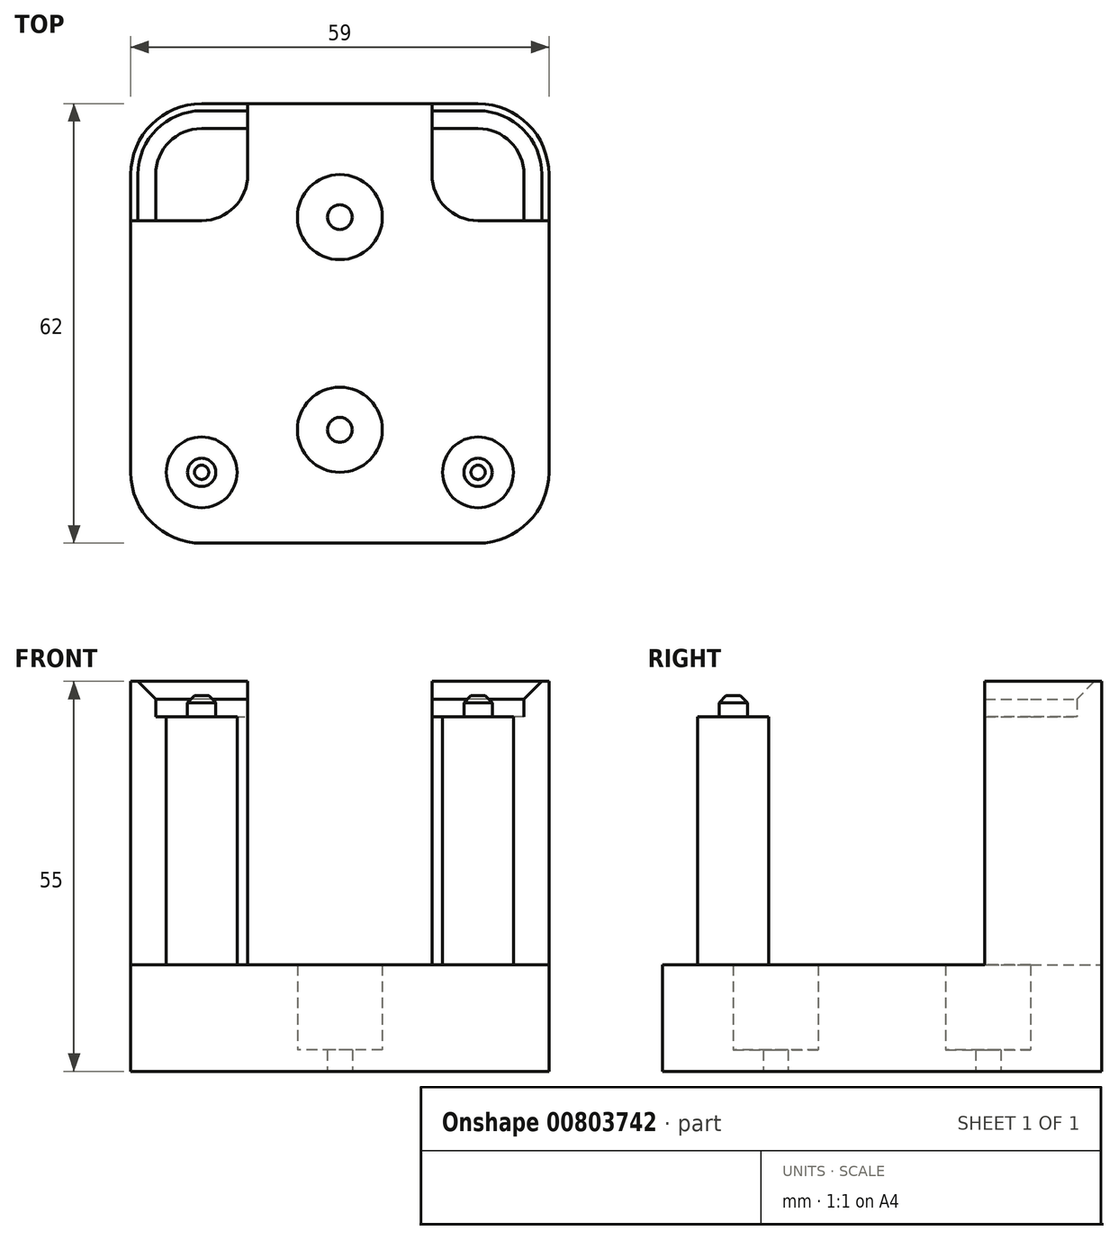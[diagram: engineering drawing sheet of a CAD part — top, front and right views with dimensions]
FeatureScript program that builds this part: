
annotation { "Feature Type Name" : "Feature", "Feature Type Description" : "" }
export const myFeature = defineFeature(function(context is Context, id is Id, definition is map)
    precondition{}
    {
        {
            var Q0;
            Q0=qCreatedBy(makeId("Top.planeOp"),FACE);
            var sketch = newSketch(context, id + "F0", { "sketchPlane" : qUnion([Q0])});
            skLineSegment(sketch, "E0.bottom", {"start": v(19.5, 31) * mm, "end": v(-19.5, 31) * mm});
            skLineSegment(sketch, "E0.top", {"start": v(19.5, -31) * mm, "end": v(-19.5, -31) * mm});
            skLineSegment(sketch, "E0.left", {"start": v(29.5, 21) * mm, "end": v(29.5, -21) * mm});
            skLineSegment(sketch, "E0.right", {"start": v(-29.5, 21) * mm, "end": v(-29.5, -21) * mm});
            skPoint(sketch, "E0.middle", {"position": v(0, 0) * mm});
            skCircle(sketch, "E1", {"center": v(19.5, -21) * mm, "radius": 2 * mm});
            skCircle(sketch, "E2", {"center": v(-19.5, 21) * mm, "radius": 6.5 * mm});
            skCircle(sketch, "E3", {"center": v(19.5, -21) * mm, "radius": 5 * mm});
            skLineSegment(sketch, "E4", {"start": v(0, 0) * mm, "end": v(0, 15) * mm});
            skCircle(sketch, "E5", {"center": v(0, 15) * mm, "radius": 6 * mm});
            skCircle(sketch, "E6", {"center": v(0, 15) * mm, "radius": 1.75 * mm});
            skLineSegment(sketch, "E7", {"start": v(0, 0) * mm, "end": v(0, -15) * mm});
            skCircle(sketch, "E8", {"center": v(0, -15) * mm, "radius": 6 * mm});
            skCircle(sketch, "E9", {"center": v(0, -15) * mm, "radius": 1.75 * mm});
            skLineSegment(sketch, "E10.bottom", {"start": v(-19.5, 21) * mm, "end": v(19.5, 21) * mm});
            skLineSegment(sketch, "E10.top", {"start": v(-19.5, -21) * mm, "end": v(19.5, -21) * mm});
            skLineSegment(sketch, "E10.left", {"start": v(-19.5, 21) * mm, "end": v(-19.5, -21) * mm});
            skLineSegment(sketch, "E10.right", {"start": v(19.5, 21) * mm, "end": v(19.5, -21) * mm});
            skLineSegment(sketch, "E11", {"start": v(0, 0) * mm, "end": v(19.5, 0) * mm});
            skPoint(sketch, "E12.visualSharp", {"position": v(-29.5, 31) * mm});
            skArc(sketch, "E12.filletArc", {"start": v(-19.5, 31) * mm, "mid": v(-26.57, 28.07) * mm, "end": v(-29.5, 21) * mm});
            skPoint(sketch, "E13.visualSharp", {"position": v(29.5, 31) * mm});
            skArc(sketch, "E13.filletArc", {"start": v(29.5, 21) * mm, "mid": v(26.57, 28.07) * mm, "end": v(19.5, 31) * mm});
            skPoint(sketch, "E14.visualSharp", {"position": v(-29.5, -31) * mm});
            skArc(sketch, "E14.filletArc", {"start": v(-29.5, -21) * mm, "mid": v(-26.57, -28.07) * mm, "end": v(-19.5, -31) * mm});
            skPoint(sketch, "E15.visualSharp", {"position": v(29.5, -31) * mm});
            skArc(sketch, "E15.filletArc", {"start": v(19.5, -31) * mm, "mid": v(26.57, -28.07) * mm, "end": v(29.5, -21) * mm});
            skLineSegment(sketch, "E16", {"start": v(-19.5, 27.5) * mm, "end": v(19.5, 27.5) * mm});
            skLineSegment(sketch, "E17", {"start": v(-19.5, 14.5) * mm, "end": v(19.5, 14.5) * mm});
            skLineSegment(sketch, "E18", {"start": v(-19.5, 14.5) * mm, "end": v(-19.5, 14.5) * mm});
            skCircle(sketch, "E19", {"center": v(-19.5, -21) * mm, "radius": 5 * mm});
            skCircle(sketch, "E20", {"center": v(-19.5, -21) * mm, "radius": 2 * mm});
            skCircle(sketch, "E21", {"center": v(19.5, 21) * mm, "radius": 6.5 * mm});
            skLineSegment(sketch, "E22", {"start": v(-13, 21) * mm, "end": v(-13, 31) * mm});
            skLineSegment(sketch, "E23", {"start": v(13, 21) * mm, "end": v(13, 31) * mm});
            skLineSegment(sketch, "E24", {"start": v(19.5, 14.5) * mm, "end": v(29.5, 14.5) * mm});
            skLineSegment(sketch, "E25", {"start": v(-19.5, 14.5) * mm, "end": v(-29.5, 14.5) * mm});
            skLineSegment(sketch, "E26", {"start": v(26, 21) * mm, "end": v(26, 14.5) * mm});
            skLineSegment(sketch, "E27", {"start": v(-26, 21) * mm, "end": v(-26, 14.5) * mm});
            skPoint(sketch, "E27.endSnap0", {"position": v(-24.5, 14.5) * mm});
            skSolve(sketch);
        }
        {
            var Q0;
            {var subQ0=sQuery(id+"F0.wireOp",EDGE,"E22");var subQ1=sQuery(id+"F0.wireOp",EDGE,"E0.bottom");var subQ2=makeQuery(id+"F0.imprint","INTERSECT",VERTEX,{"derivedFrom":[subQ1,subQ0]});Q0=makeQuery(id+"F0.imprint","IMPRINT",FACE,{"disambiguationData":[TD([[makeQuery(id+"F0.imprint","IMPRINT",EDGE,{"disambiguationData":[TD([[subQ2,1.0]])],"derivedFrom":subQ1}),1.0]])]});}
            var Q1;
            Q1=makeQuery(id+"F0.imprint","IMPRINT",FACE,{"disambiguationData":[TD([[makeQuery(id+"F0.imprint","IMPRINT",EDGE,{"derivedFrom":sQuery(id+"F0.wireOp",EDGE,"E0.top")}),-1.0]])]});
            var Q2;
            {var subQ0=sQuery(id+"F0.wireOp",EDGE,"E11");Q2=makeQuery(id+"F0.imprint","IMPRINT",FACE,{"disambiguationData":[TD([[makeQuery(id+"F0.imprint","IMPRINT",EDGE,{"derivedFrom":subQ0}),1.0]])]});}
            var Q3;
            {var subQ1=sQuery(id+"F0.wireOp",EDGE,"E4");var subQ5=sQuery(id+"F0.wireOp",EDGE,"E5");var subQ6=makeQuery(id+"F0.imprint","INTERSECT",VERTEX,{"derivedFrom":[subQ1,subQ5]});Q3=makeQuery(id+"F0.imprint","IMPRINT",FACE,{"disambiguationData":[TD([[makeQuery(id+"F0.imprint","IMPRINT",EDGE,{"disambiguationData":[TD([[subQ6,1.0]])],"derivedFrom":subQ5}),-1.0]])]});}
            var Q4;
            {var subQ0=sQuery(id+"F0.wireOp",EDGE,"E11");Q4=makeQuery(id+"F0.imprint","IMPRINT",FACE,{"disambiguationData":[TD([[makeQuery(id+"F0.imprint","IMPRINT",EDGE,{"derivedFrom":subQ0}),-1.0]])]});}
            var Q5;
            {var subQ0=sQuery(id+"F0.wireOp",EDGE,"Fgb9CfrY-dhn4-4UBN-2pW2-9sD9XJII3xpJ");Q5=makeQuery(id+"F0.imprint","IMPRINT",FACE,{"disambiguationData":[TD([[makeQuery(id+"F0.imprint","IMPRINT",EDGE,{"derivedFrom":subQ0}),1.0]])]});}
            var Q6;
            {var subQ3=sQuery(id+"F0.wireOp",EDGE,"E19");var subQ5=sQuery(id+"F0.wireOp",EDGE,"bsxKk5JZ-FVBb-cfbX-uEi1-lJpJewRCnain");var subQ6=makeQuery(id+"F0.imprint","INTERSECT",VERTEX,{"derivedFrom":[subQ5,subQ3]});Q6=makeQuery(id+"F0.imprint","IMPRINT",FACE,{"disambiguationData":[TD([[makeQuery(id+"F0.imprint","IMPRINT",EDGE,{"disambiguationData":[TD([[subQ6,1.0]])],"derivedFrom":subQ5}),1.0]])]});}
            var Q7;
            {var subQ0=sQuery(id+"F0.wireOp",EDGE,"E22");var subQ1=sQuery(id+"F0.wireOp",EDGE,"E16");var subQ2=makeQuery(id+"F0.imprint","INTERSECT",VERTEX,{"derivedFrom":[subQ1,subQ0]});Q7=makeQuery(id+"F0.imprint","IMPRINT",FACE,{"disambiguationData":[TD([[makeQuery(id+"F0.imprint","IMPRINT",EDGE,{"disambiguationData":[TD([[subQ2,-1.0]])],"derivedFrom":subQ1}),-1.0]])]});}
            var Q8;
            {var subQ0=sQuery(id+"F0.wireOp",EDGE,"Rvfl0PQZ-DZTq-9wpm-qxsT-ofNjnk88OBcv");var subQ1=sQuery(id+"F0.wireOp",EDGE,"E3");var subQ2=makeQuery(id+"F0.imprint","INTERSECT",VERTEX,{"derivedFrom":[subQ1,subQ0]});Q8=makeQuery(id+"F0.imprint","IMPRINT",FACE,{"disambiguationData":[TD([[makeQuery(id+"F0.imprint","IMPRINT",EDGE,{"disambiguationData":[TD([[subQ2,-1.0]])],"derivedFrom":subQ1}),-1.0]])]});}
            var Q9;
            {var subQ0=sQuery(id+"F0.wireOp",EDGE,"E17");var subQ5=sQuery(id+"F0.wireOp",EDGE,"E5");var subQ6=makeQuery(id+"F0.imprint","INTERSECT",VERTEX,{"disambiguationData":[OD(0.0)],"derivedFrom":[subQ5,subQ0]});Q9=makeQuery(id+"F0.imprint","IMPRINT",FACE,{"disambiguationData":[TD([[makeQuery(id+"F0.imprint","IMPRINT",EDGE,{"disambiguationData":[TD([[subQ6,1.0]])],"derivedFrom":subQ5}),-1.0]])]});}
            var Q10;
            {var subQ0=sQuery(id+"F0.wireOp",EDGE,"E10.bottom");var subQ1=sQuery(id+"F0.wireOp",EDGE,"E5");var subQ2=makeQuery(id+"F0.imprint","INTERSECT",VERTEX,{"derivedFrom":[subQ1,subQ0]});Q10=makeQuery(id+"F0.imprint","IMPRINT",FACE,{"disambiguationData":[TD([[makeQuery(id+"F0.imprint","IMPRINT",EDGE,{"disambiguationData":[TD([[subQ2,1.0]])],"derivedFrom":subQ1}),-1.0]])]});}
            extrude(context, id + "F1", {"entities" : qUnion([Q0, Q1, Q2, Q3, Q4, Q5, Q6, Q7, Q8, Q9, Q10]), "depth" : 15 * mm, "offsetDistance" : 25 * mm});
        }
        {
            var Q0;
            {var subQ0=sQuery(id+"F0.wireOp",EDGE,"E2");var subQ1=makeQuery(id+"F0.imprint","INTERSECT",VERTEX,{"derivedFrom":[subQ0,sQuery(id+"F0.wireOp",EDGE,"E16")]});Q0=makeQuery(id+"F0.imprint","IMPRINT",FACE,{"disambiguationData":[TD([[makeQuery(id+"F0.imprint","IMPRINT",EDGE,{"disambiguationData":[TD([[subQ1,1.0]])],"derivedFrom":subQ0}),1.0]])]});}
            var Q1;
            {var subQ0=sQuery(id+"F0.wireOp",EDGE,"E10.left");var subQ3=sQuery(id+"F0.wireOp",EDGE,"E10.bottom");var subQ5=makeQuery(id+"F0.imprint","INTERSECT",VERTEX,{"derivedFrom":[subQ3,subQ0]});Q1=makeQuery(id+"F0.imprint","IMPRINT",FACE,{"disambiguationData":[TD([[makeQuery(id+"F0.imprint","IMPRINT",EDGE,{"disambiguationData":[TD([[subQ5,-1.0]])],"derivedFrom":subQ3}),-1.0]])]});}
            var Q2;
            {var subQ0=sQuery(id+"F0.wireOp",EDGE,"E16");var subQ1=sQuery(id+"F0.wireOp",EDGE,"E2");var subQ2=makeQuery(id+"F0.imprint","INTERSECT",VERTEX,{"derivedFrom":[subQ1,subQ0]});Q2=makeQuery(id+"F0.imprint","IMPRINT",FACE,{"disambiguationData":[TD([[makeQuery(id+"F0.imprint","IMPRINT",EDGE,{"disambiguationData":[TD([[subQ2,-1.0]])],"derivedFrom":subQ0}),-1.0]])]});}
            var Q3;
            {var subQ0=sQuery(id+"F0.wireOp",EDGE,"E21");var subQ1=makeQuery(id+"F0.imprint","INTERSECT",VERTEX,{"derivedFrom":[sQuery(id+"F0.wireOp",EDGE,"E16"),subQ0]});Q3=makeQuery(id+"F0.imprint","IMPRINT",FACE,{"disambiguationData":[TD([[makeQuery(id+"F0.imprint","IMPRINT",EDGE,{"disambiguationData":[TD([[subQ1,1.0]])],"derivedFrom":subQ0}),1.0]])]});}
            var Q4;
            {var subQ0=sQuery(id+"F0.wireOp",EDGE,"E10.right");var subQ1=sQuery(id+"F0.wireOp",EDGE,"E10.bottom");var subQ2=makeQuery(id+"F0.imprint","INTERSECT",VERTEX,{"derivedFrom":[subQ1,subQ0]});Q4=makeQuery(id+"F0.imprint","IMPRINT",FACE,{"disambiguationData":[TD([[makeQuery(id+"F0.imprint","IMPRINT",EDGE,{"disambiguationData":[TD([[subQ2,1.0]])],"derivedFrom":subQ1}),-1.0]])]});}
            var Q5;
            {var subQ0=sQuery(id+"F0.wireOp",EDGE,"E10.top");var subQ1=sQuery(id+"F0.wireOp",EDGE,"E1");var subQ2=makeQuery(id+"F0.imprint","INTERSECT",VERTEX,{"derivedFrom":[subQ1,subQ0]});Q5=makeQuery(id+"F0.imprint","IMPRINT",FACE,{"disambiguationData":[TD([[makeQuery(id+"F0.imprint","IMPRINT",EDGE,{"disambiguationData":[TD([[subQ2,-1.0]])],"derivedFrom":subQ1}),-1.0]])]});}
            var Q6;
            {var subQ0=sQuery(id+"F0.wireOp",EDGE,"E10.top");var subQ1=sQuery(id+"F0.wireOp",EDGE,"E1");var subQ2=makeQuery(id+"F0.imprint","INTERSECT",VERTEX,{"derivedFrom":[subQ1,subQ0]});Q6=makeQuery(id+"F0.imprint","IMPRINT",FACE,{"disambiguationData":[TD([[makeQuery(id+"F0.imprint","IMPRINT",EDGE,{"disambiguationData":[TD([[subQ2,1.0]])],"derivedFrom":subQ1}),-1.0]])]});}
            var Q7;
            {var subQ0=sQuery(id+"F0.wireOp",EDGE,"E20");var subQ1=sQuery(id+"F0.wireOp",EDGE,"E10.top");var subQ2=makeQuery(id+"F0.imprint","INTERSECT",VERTEX,{"derivedFrom":[subQ1,subQ0]});Q7=makeQuery(id+"F0.imprint","IMPRINT",FACE,{"disambiguationData":[TD([[makeQuery(id+"F0.imprint","IMPRINT",EDGE,{"disambiguationData":[TD([[subQ2,-1.0]])],"derivedFrom":subQ1}),-1.0]])]});}
            var Q8;
            {var subQ0=sQuery(id+"F0.wireOp",EDGE,"E20");var subQ1=sQuery(id+"F0.wireOp",EDGE,"E10.top");var subQ2=makeQuery(id+"F0.imprint","INTERSECT",VERTEX,{"derivedFrom":[subQ1,subQ0]});Q8=makeQuery(id+"F0.imprint","IMPRINT",FACE,{"disambiguationData":[TD([[makeQuery(id+"F0.imprint","IMPRINT",EDGE,{"disambiguationData":[TD([[subQ2,-1.0]])],"derivedFrom":subQ1}),1.0]])]});}
            var Q9;
            {var subQ0=sQuery(id+"F0.wireOp",EDGE,"E21");var subQ1=sQuery(id+"F0.wireOp",EDGE,"E16");var subQ2=makeQuery(id+"F0.imprint","INTERSECT",VERTEX,{"derivedFrom":[subQ1,subQ0]});Q9=makeQuery(id+"F0.imprint","IMPRINT",FACE,{"disambiguationData":[TD([[makeQuery(id+"F0.imprint","IMPRINT",EDGE,{"disambiguationData":[TD([[subQ2,1.0]])],"derivedFrom":subQ1}),-1.0]])]});}
            var Q10;
            {var subQ3=sQuery(id+"F0.wireOp",EDGE,"E26");Q10=makeQuery(id+"F0.imprint","IMPRINT",FACE,{"disambiguationData":[TD([[makeQuery(id+"F0.imprint","IMPRINT",EDGE,{"derivedFrom":subQ3}),-1.0]])]});}
            var Q11;
            {var subQ3=sQuery(id+"F0.wireOp",EDGE,"E27");Q11=makeQuery(id+"F0.imprint","IMPRINT",FACE,{"disambiguationData":[TD([[makeQuery(id+"F0.imprint","IMPRINT",EDGE,{"derivedFrom":subQ3}),1.0]])]});}
            extrude(context, id + "F2", {"entities" : qUnion([Q0, Q1, Q2, Q3, Q4, Q5, Q6, Q7, Q8, Q9, Q10, Q11]), "operationType" : NewBodyOperationType.ADD, "depth" : 50 * mm, "offsetDistance" : 25 * mm});
        }
        {
            var Q0;
            {var subQ0=sQuery(id+"F0.wireOp",EDGE,"E10.left");var subQ1=sQuery(id+"F0.wireOp",EDGE,"E10.top");var subQ2=makeQuery(id+"F0.imprint","INTERSECT",VERTEX,{"derivedFrom":[subQ1,subQ0]});Q0=makeQuery(id+"F0.imprint","IMPRINT",FACE,{"disambiguationData":[TD([[makeQuery(id+"F0.imprint","IMPRINT",EDGE,{"disambiguationData":[TD([[subQ2,-1.0]])],"derivedFrom":subQ1}),-1.0]])]});}
            var Q1;
            {var subQ0=sQuery(id+"F0.wireOp",EDGE,"E10.left");var subQ1=sQuery(id+"F0.wireOp",EDGE,"E10.top");var subQ2=makeQuery(id+"F0.imprint","INTERSECT",VERTEX,{"derivedFrom":[subQ1,subQ0]});Q1=makeQuery(id+"F0.imprint","IMPRINT",FACE,{"disambiguationData":[TD([[makeQuery(id+"F0.imprint","IMPRINT",EDGE,{"disambiguationData":[TD([[subQ2,-1.0]])],"derivedFrom":subQ1}),1.0]])]});}
            var Q2;
            {var subQ0=sQuery(id+"F0.wireOp",EDGE,"E10.top");var subQ1=sQuery(id+"F0.wireOp",EDGE,"E1");var subQ2=makeQuery(id+"F0.imprint","INTERSECT",VERTEX,{"derivedFrom":[subQ1,subQ0]});Q2=makeQuery(id+"F0.imprint","IMPRINT",FACE,{"disambiguationData":[TD([[makeQuery(id+"F0.imprint","IMPRINT",EDGE,{"disambiguationData":[TD([[subQ2,1.0]])],"derivedFrom":subQ1}),1.0]])]});}
            var Q3;
            {var subQ0=sQuery(id+"F0.wireOp",EDGE,"E10.top");var subQ1=sQuery(id+"F0.wireOp",EDGE,"E1");var subQ2=makeQuery(id+"F0.imprint","INTERSECT",VERTEX,{"derivedFrom":[subQ1,subQ0]});Q3=makeQuery(id+"F0.imprint","IMPRINT",FACE,{"disambiguationData":[TD([[makeQuery(id+"F0.imprint","IMPRINT",EDGE,{"disambiguationData":[TD([[subQ2,-1.0]])],"derivedFrom":subQ1}),1.0]])]});}
            extrude(context, id + "F3", {"entities" : qUnion([Q0, Q1, Q2, Q3]), "operationType" : NewBodyOperationType.ADD, "depth" : 53 * mm, "offsetDistance" : 25 * mm});
        }
        {
            var Q0;
            Q0=makeQuery(id+"F0.imprint","IMPRINT",FACE,{"disambiguationData":[TD([[makeQuery(id+"F0.imprint","IMPRINT",EDGE,{"derivedFrom":sQuery(id+"F0.wireOp",EDGE,"E6")}),-1.0]])]});
            var Q1;
            Q1=makeQuery(id+"F0.imprint","IMPRINT",FACE,{"disambiguationData":[TD([[makeQuery(id+"F0.imprint","IMPRINT",EDGE,{"derivedFrom":sQuery(id+"F0.wireOp",EDGE,"E9")}),-1.0]])]});
            var Q2;
            {var subQ0=sQuery(id+"F0.wireOp",EDGE,"E17");var subQ1=sQuery(id+"F0.wireOp",EDGE,"E5");var subQ2=makeQuery(id+"F0.imprint","INTERSECT",VERTEX,{"disambiguationData":[OD(0.0)],"derivedFrom":[subQ1,subQ0]});Q2=makeQuery(id+"F0.imprint","IMPRINT",FACE,{"disambiguationData":[TD([[makeQuery(id+"F0.imprint","IMPRINT",EDGE,{"disambiguationData":[TD([[subQ2,1.0]])],"derivedFrom":subQ1}),1.0]])]});}
            extrude(context, id + "F4", {"entities" : qUnion([Q0, Q1, Q2]), "operationType" : NewBodyOperationType.ADD, "depth" : 3 * mm, "offsetDistance" : 25 * mm});
        }
        {
            var Q0;
            {var subQ5=sQuery(id+"F0.wireOp",EDGE,"E13.filletArc");Q0=makeQuery(id+"F0.imprint","IMPRINT",FACE,{"disambiguationData":[TD([[makeQuery(id+"F0.imprint","IMPRINT",EDGE,{"derivedFrom":subQ5}),1.0]])]});}
            var Q1;
            {var subQ0=sQuery(id+"F0.wireOp",EDGE,"E12.filletArc");Q1=makeQuery(id+"F0.imprint","IMPRINT",FACE,{"disambiguationData":[TD([[makeQuery(id+"F0.imprint","IMPRINT",EDGE,{"derivedFrom":subQ0}),1.0]])]});}
            extrude(context, id + "F5", {"entities" : qUnion([Q0, Q1]), "operationType" : NewBodyOperationType.ADD, "depth" : 55 * mm, "offsetDistance" : 25 * mm});
        }
        {
            var Q0;
            Q0=makeQuery(id+"F5.opExtrude","CAP_EDGE",EDGE,{"disambiguationData":[OSD([sQuery(id+"F0.wireOp",EDGE,"E21")])],"isStart":false});
            var Q1;
            {var subQ0=sQuery(id+"F0.wireOp",EDGE,"E16");Q1=makeQuery(id+"F5.opExtrude","CAP_EDGE",EDGE,{"disambiguationData":[OSD([subQ0]),TDD([makeQuery(id+"F0.imprint","IMPRINT",EDGE,{"disambiguationData":[TD([[makeQuery(id+"F0.imprint","INTERSECT",VERTEX,{"derivedFrom":[subQ0,sQuery(id+"F0.wireOp",EDGE,"E21")]}),1.0]])],"derivedFrom":subQ0})])],"isStart":false});}
            var Q2;
            Q2=makeQuery(id+"F5.opExtrude","CAP_EDGE",EDGE,{"disambiguationData":[OSD([sQuery(id+"F0.wireOp",EDGE,"Rvfl0PQZ-DZTq-9wpm-qxsT-ofNjnk88OBcv")])],"isStart":false});
            var Q3;
            {var subQ0=sQuery(id+"F0.wireOp",EDGE,"E16");Q3=makeQuery(id+"F5.opExtrude","CAP_EDGE",EDGE,{"disambiguationData":[OSD([subQ0]),TDD([makeQuery(id+"F0.imprint","IMPRINT",EDGE,{"disambiguationData":[TD([[makeQuery(id+"F0.imprint","INTERSECT",VERTEX,{"derivedFrom":[sQuery(id+"F0.wireOp",EDGE,"E2"),subQ0]}),-1.0]])],"derivedFrom":subQ0})])],"isStart":false});}
            var Q4;
            Q4=makeQuery(id+"F5.opExtrude","CAP_EDGE",EDGE,{"disambiguationData":[OSD([sQuery(id+"F0.wireOp",EDGE,"E2")])],"isStart":false});
            var Q5;
            Q5=makeQuery(id+"F5.opExtrude","CAP_EDGE",EDGE,{"disambiguationData":[OSD([sQuery(id+"F0.wireOp",EDGE,"bsxKk5JZ-FVBb-cfbX-uEi1-lJpJewRCnain")])],"isStart":false});
            chamfer(context, id + "F6", {"entities" : qUnion([Q0, Q1, Q2, Q3, Q4, Q5]), "width" : 2.5 * mm, "tangentPropagation" : true});
        }
        {
            var Q0;
            Q0=makeQuery(id+"F3.opExtrude","CAP_FACE",FACE,{"disambiguationData":[OSD([sQuery(id+"F0.wireOp",EDGE,"E20")])],"isStart":false});
            var Q1;
            Q1=makeQuery(id+"F3.opExtrude","CAP_FACE",FACE,{"disambiguationData":[OSD([sQuery(id+"F0.wireOp",EDGE,"E1")])],"isStart":false});
            chamfer(context, id + "F7", {"entities" : qUnion([Q0, Q1]), "width" : 1 * mm, "tangentPropagation" : true});
        }
    });
